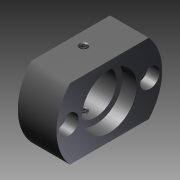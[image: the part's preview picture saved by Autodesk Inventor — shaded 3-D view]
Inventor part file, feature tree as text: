
AUTODESK INVENTOR PART (.ipt)
format: ipt  version: 2011 SP1 (Build 150282100, 282)  size: 157,184 bytes
history: native  units: mm
features: other x21, sketch x5, revolve x4, thread x3, extrude x1, pattern_linear x1
ambient origin geometry x8: Origin, YZ Plane, XZ Plane, XY Plane, X Axis, Y Axis, Z Axis, Center Point
bodies: Solid1 (feature_tree)
feature tree (35):
  revolve  "Revolution1"  [1 undecoded]
  extrude  "Extrusion1"  Depth=14.147mm TaperAngle=0.0deg
  revolve  "Revolution2"  Angle=360.0deg
  thread  "Thread1"  [1 undecoded]
  pattern_linear  "Rectangular Pattern1"  Spacing1=0.0mm  [1 undecoded]
  revolve  "Revolution3"  [1 undecoded]
  thread  "Thread2"  [1 undecoded]
  revolve  "Revolution4"  [1 undecoded]
  thread  "Thread3"  [1 undecoded]
  other  "to_bearings_XY"
  other  "to_bearings_YZ"
  other  "to_bearings_ZX"
  other  "to_bearings_X"
  other  "to_bearings_Y"
  other  "to_bearings_Z"
  other  "to_bearings_Center"
  other  "to_screw1_XY"
  other  "to_screw1_YZ"
  other  "to_screw1_ZX"
  other  "to_screw1_X"
  other  "to_screw1_Y"
  other  "to_screw1_Z"
  other  "to_screw1_Center"
  other  "to_screw2_XY"
  other  "to_screw2_YZ"
  other  "to_screw2_ZX"
  other  "to_screw2_X"
  other  "to_screw2_Y"
  other  "to_screw2_Z"
  other  "to_screw2_Center"
  sketch  "Sketch_1"  dims[d0=360.0deg d1=24.0mm d2=0.0mm]
  sketch  "Sketch_2"  dims[d3=360.0deg d4=14.147mm d5=0.0mm]
  sketch  "Sketch_3"  dims[d6=20.0mm d8=46.0mm d9=10.0mm d11=0.0mm d12=360.0deg d13=7.484mm d14=0.0mm]
  sketch  "Sketch_4"  dims[d15=360.0deg]
  sketch  "Sketch_6"  dims[d16=7.484mm d17=0.0mm d18=0.0mm]
note: 7 required parameter values undecoded (feature->parameter linkage not recoverable at this tier; creation-order binding heuristic only, values carry confidence <= 0.55)